# Revit family: NAU_Naughtone_Stng_Symbol_Bench
name_source: partatom
category: Furniture
revit_build: Autodesk Revit 2018 (Build: 20170223_1515(x64)
units: mm (PartAtom-declared; Revit-internal decimal feet)

## family parameters
Always vertical = Yes
Cut with Voids When Loaded = No
OmniClass Number = 23.40.20.00
OmniClass Title = General Furniture and Specialties
Room Calculation Point = No
Shared = Yes
Work Plane-Based = No

## types (6) — shared parameters
Assembly Code = E2020200
AssetType = Moveable
BIMObjectName = Naughtone_Seating_Symbol_Bench
CodePerformance = BS EN 16139:2013
Color = Various
DurationUnit = year
Finish = Fabric upholstery
IfcExportAs = IfcFurnishingElementType
MainColor = Various
ManufacturerAddress = Knaresborough Tech Park, Manse Lane, Knaresborough, HG5 8LF
ManufacturerName = Naughtone
ManufacturerURL = www.naughtone.com
Material = Legs in 16 RAL Colours, Oak, or Walnut
NBSDescription = Seating
NBSReference = 45-35-72/352
Name = Seating_Symbol_Bench_Naughtone
NominalHeight = 410 mm  [stored 1.34514 ft]
ProductInformation = www.naughtone.com/portfolio-view/symbol
SustainabilityPerformance = FSC certified. FISP certified. ISO 14001 certified
URL = www.naughtone.com
Version = 1
WarrantyDescription = Request warranty information from naughtone
WarrantyDurationLabor = 7
WarrantyDurationParts = 7
WarrantyDurationUnit = year

## per-type parameters (varying)
- SYM1ST - Symbol Single Stool: Category=Pr_40_50_12_85 : Stools; Description=Symbol Single Stool; IfcExportType=STOOL; Is2Seat=No; Is3Seat=No; IsBackLeg=Yes; IsBench=Yes; IsRectangular=Yes; IsSYM180BEN=No; IsSYMQBEN=No; IsTable=No; Keynote=Pr_40_50_12_85; LeftOffset=255 mm  [stored 0.836614 ft]; Model=SYM1ST; ModelNumber=SYM1ST; ModelReference=Symbol Single Stool; NominalLength=510 mm  [stored 1.67323 ft]; NominalWidth=510 mm  [stored 1.67323 ft]; RightOffset=255 mm  [stored 0.836614 ft]; Shape=Square; Size=510 x 510 x 410mm; Uniclass2015Code=Pr_40_50_12_85; Uniclass2015Title=Stools; VoidOffset2Seat=10 mm  [stored 0.0328084 ft]; VoidOffset3Seat=10 mm  [stored 0.0328084 ft]
- SYM2BEN - Symbol 2 Seat Bench: Category=Pr_40_50_12_07 : Benches; Description=Symbol 2 Seat Bench; IfcExportType=BENCH; Is2Seat=Yes; Is3Seat=No; IsBackLeg=Yes; IsBench=Yes; IsRectangular=Yes; IsSYM180BEN=No; IsSYMQBEN=No; IsTable=No; Keynote=Pr_40_50_12_07; LeftOffset=510 mm  [stored 1.67323 ft]; Model=SYM2BEN; ModelNumber=SYM2BEN; ModelReference=Symbol 2 Seat Bench; NominalLength=1020 mm  [stored 3.34646 ft]; NominalWidth=510 mm  [stored 1.67323 ft]; RightOffset=510 mm  [stored 1.67323 ft]; Shape=Rectangular; Size=1020 x 510 x 410mm; Uniclass2015Code=Pr_40_50_12_07; Uniclass2015Title=Benches; VoidOffset2Seat=0 mm  [stored 0 ft]; VoidOffset3Seat=10 mm  [stored 0.0328084 ft]
- SYM3BEN Symbol 3 Seat Bench: Category=Pr_40_50_12_07 : Benches; Description=Symbol 3 Seat Bench; IfcExportType=BENCH; Is2Seat=Yes; Is3Seat=Yes; IsBackLeg=Yes; IsBench=Yes; IsRectangular=Yes; IsSYM180BEN=No; IsSYMQBEN=No; IsTable=No; Keynote=Pr_40_50_12_07; LeftOffset=765 mm  [stored 2.50984 ft]; Model=SYM3BEN; ModelNumber=SYM3BEN; ModelReference=Symbol 3 Seat Bench; NominalLength=1530 mm  [stored 5.01969 ft]; NominalWidth=510 mm  [stored 1.67323 ft]; RightOffset=765 mm  [stored 2.50984 ft]; Shape=Rectangular; Size=1530 x 510 x 410mm; Uniclass2015Code=Pr_40_50_12_07; Uniclass2015Title=Benches; VoidOffset2Seat=0 mm  [stored 0 ft]; VoidOffset3Seat=0 mm  [stored 0 ft]
- HATSYMTREC - Symbol Rectangular Table: Category=Pr_40_50_21 : Desks, tables and worktops; Description=Hatch / Symbol Rectangular Table; Features=White or Black MFMDF top; or Oak or Walnut veneer top. Matching edge detail; IfcExportType=BENCH; Is2Seat=No; Is3Seat=No; IsBackLeg=Yes; IsBench=No; IsRectangular=Yes; IsSYM180BEN=No; IsSYMQBEN=No; IsTable=Yes; Keynote=Pr_40_50_21; LeftOffset=345 mm  [stored 1.13189 ft]; Model=HATSYMTREC; ModelNumber=HATSYMTREC; ModelReference=Hatch / Symbol Rectangular Table; NominalLength=690 mm  [stored 2.26378 ft]; NominalWidth=510 mm  [stored 1.67323 ft]; RightOffset=345 mm  [stored 1.13189 ft]; Shape=Rectangular; Size=690 x 510 x 410mm; Uniclass2015Code=Pr_40_50_21; Uniclass2015Title=Desks, tables and worktops; VoidOffset2Seat=10 mm  [stored 0.0328084 ft]; VoidOffset3Seat=10 mm  [stored 0.0328084 ft]
- SYMQBEN - Symbol Quarter Circle Bench: Category=Pr_40_50_12_07 : Benches; Description=Symbol Quarter Circle Bench; IfcExportType=BENCH; Is2Seat=No; Is3Seat=No; IsBackLeg=Yes; IsBench=No; IsRectangular=No; IsSYM180BEN=No; IsSYMQBEN=Yes; IsTable=No; Keynote=Pr_40_50_12_07; LeftOffset=345 mm  [stored 1.13189 ft]; Model=SYMQBEN; ModelNumber=SYMQBEN; ModelReference=Symbol Quarter Circle Bench; NominalLength=690 mm  [stored 2.26378 ft]; NominalWidth=690 mm  [stored 2.26378 ft]; RightOffset=345 mm  [stored 1.13189 ft]; Shape=Rectangular; Size=690 x 690 x 410mm; Uniclass2015Code=Pr_40_50_12_07; Uniclass2015Title=Benches; VoidOffset2Seat=10 mm  [stored 0.0328084 ft]; VoidOffset3Seat=10 mm  [stored 0.0328084 ft]
- SYM180BEN - Symbol 180º Bench: Category=Pr_40_50_12_07 : Benches; Description=Symbol 180º Bench; IfcExportType=BENCH; Is2Seat=No; Is3Seat=No; IsBackLeg=No; IsBench=No; IsRectangular=No; IsSYM180BEN=Yes; IsSYMQBEN=No; IsTable=No; Keynote=Pr_40_50_12_07; LeftOffset=345 mm  [stored 1.13189 ft]; Model=SYM180BEN; ModelNumber=SYM180BEN; ModelReference=Symbol 180º Bench; NominalLength=690 mm  [stored 2.26378 ft]; NominalWidth=1380 mm  [stored 4.52756 ft]; RightOffset=345 mm  [stored 1.13189 ft]; Shape=Semi-circular; Size=1380 x 690 x 410mm; Uniclass2015Code=Pr_40_50_12_07; Uniclass2015Title=Benches; VoidOffset2Seat=10 mm  [stored 0.0328084 ft]; VoidOffset3Seat=10 mm  [stored 0.0328084 ft]

note: [stored X ft] marks values corroborated as IEEE doubles in the binary element streams (Revit-internal decimal feet)

## geometry (parser evidence)
native form markers: Sweep x3
no freeform markers — native parametric forms only
